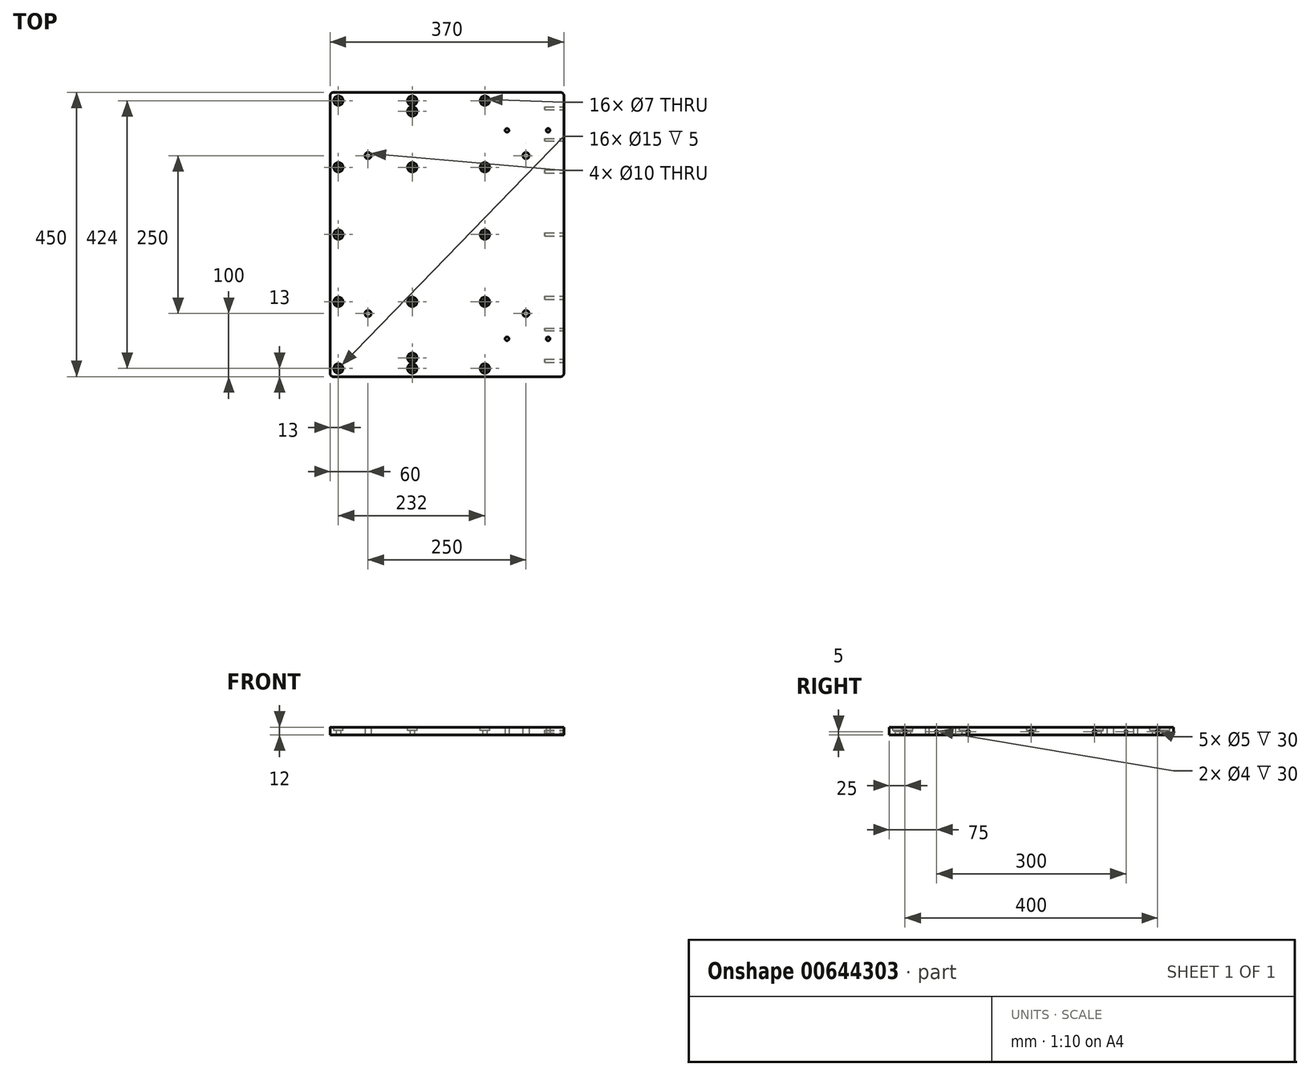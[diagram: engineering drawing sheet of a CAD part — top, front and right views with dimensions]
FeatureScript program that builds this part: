
annotation { "Feature Type Name" : "Feature", "Feature Type Description" : "" }
export const myFeature = defineFeature(function(context is Context, id is Id, definition is map)
    precondition{}
    {
        {
            var Q0;
            Q0=qCreatedBy(makeId("Top.planeOp"),FACE);
            var sketch = newSketch(context, id + "F0", { "sketchPlane" : qUnion([Q0])});
            skLineSegment(sketch, "E0.bottom", {"start": v(185, 225) * mm, "end": v(-185, 225) * mm});
            skLineSegment(sketch, "E0.top", {"start": v(185, -225) * mm, "end": v(-185, -225) * mm});
            skLineSegment(sketch, "E0.left", {"start": v(185, 225) * mm, "end": v(185, -225) * mm});
            skLineSegment(sketch, "E0.right", {"start": v(-185, 225) * mm, "end": v(-185, -225) * mm});
            skPoint(sketch, "E0.middle", {"position": v(0, 0) * mm});
            skLineSegment(sketch, "E1", {"start": v(0, 194.9) * mm, "end": v(0, -168.69) * mm, "construction": true});
            skSolve(sketch);
        }
        {
            var Q0;
            Q0 = qSketchRegion(id + "F0", true);
            extrude(context, id + "F1", {"entities" : qUnion([Q0]), "depth" : 12 * mm, "offsetDistance" : 25 * mm});
        }
        {
            var Q0;
            Q0=qCreatedBy(makeId("Top.planeOp"),FACE);
            var sketch = newSketch(context, id + "F2", { "sketchPlane" : qUnion([Q0])});
            skCircle(sketch, "E2", {"center": v(-172, 106.5) * mm, "radius": 3.5 * mm});
            skCircle(sketch, "E3", {"center": v(-172, 0) * mm, "radius": 3.5 * mm});
            skCircle(sketch, "E4", {"center": v(-172, -332.14) * mm, "radius": 2.87 * mm});
            skLineSegment(sketch, "E5", {"start": v(-172, 212) * mm, "end": v(-172, -289.23) * mm, "construction": true});
            skCircle(sketch, "E6", {"center": v(60, 106.5) * mm, "radius": 3.5 * mm});
            skCircle(sketch, "E7", {"center": v(60, 0) * mm, "radius": 3.5 * mm});
            skCircle(sketch, "E8", {"center": v(60, -212) * mm, "radius": 3.5 * mm});
            skLineSegment(sketch, "E9", {"start": v(60, 212) * mm, "end": v(60, -297.69) * mm, "construction": true});
            skLineSegment(sketch, "E10", {"start": v(213.74, 212) * mm, "end": v(-227.82, 212) * mm, "construction": true});
            skLineSegment(sketch, "E11", {"start": v(213.74, 106.5) * mm, "end": v(-243.05, 106.5) * mm, "construction": true});
            skCircle(sketch, "E12", {"center": v(60, 212) * mm, "radius": 3.5 * mm});
            skCircle(sketch, "E13", {"center": v(-172, 212) * mm, "radius": 3.5 * mm});
            skCircle(sketch, "E14", {"center": v(-172, -106.5) * mm, "radius": 3.5 * mm});
            skCircle(sketch, "E15", {"center": v(-172, -212) * mm, "radius": 3.5 * mm});
            skCircle(sketch, "E16", {"center": v(60, -106.5) * mm, "radius": 3.5 * mm});
            skLineSegment(sketch, "E17", {"start": v(-279.8, -212) * mm, "end": v(194.38, -212) * mm, "construction": true});
            skLineSegment(sketch, "E18", {"start": v(-279.8, -106.5) * mm, "end": v(196.56, -106.5) * mm, "construction": true});
            skCircle(sketch, "E19", {"center": v(-55, 212) * mm, "radius": 3.5 * mm});
            skCircle(sketch, "E20", {"center": v(-55, -212) * mm, "radius": 3.5 * mm});
            skCircle(sketch, "E21", {"center": v(-55, -106.5) * mm, "radius": 3.5 * mm});
            skCircle(sketch, "E22", {"center": v(-55, 106.5) * mm, "radius": 3.5 * mm});
            skLineSegment(sketch, "E23", {"start": v(-55, 255.47) * mm, "end": v(-55, -293.36) * mm, "construction": true});
            skLineSegment(sketch, "E24", {"start": v(-233.42, 165) * mm, "end": v(273.44, 165) * mm, "construction": true});
            skLineSegment(sketch, "E25", {"start": v(-281.7, -165) * mm, "end": v(222.11, -165) * mm, "construction": true});
            skCircle(sketch, "E26", {"center": v(160, -165) * mm, "radius": 3 * mm});
            skCircle(sketch, "E27", {"center": v(160, 165) * mm, "radius": 3 * mm});
            skCircle(sketch, "E28", {"center": v(95, -165) * mm, "radius": 3 * mm});
            skCircle(sketch, "E29", {"center": v(95, 165) * mm, "radius": 3 * mm});
            skLineSegment(sketch, "E30", {"start": v(211.65, 0) * mm, "end": v(-280.45, 0) * mm, "construction": true});
            skCircle(sketch, "E31", {"center": v(-55, 195) * mm, "radius": 3.5 * mm});
            skCircle(sketch, "E32", {"center": v(-55, -195) * mm, "radius": 3.5 * mm});
            skSolve(sketch);
        }
        {
            var Q0;
            Q0 = qSketchRegion(id + "F2", true);
            extrude(context, id + "F3", {"entities" : qUnion([Q0]), "operationType" : NewBodyOperationType.REMOVE, "endBound" : BoundingType.THROUGH_ALL, "depth" : 25 * mm, "offsetDistance" : 25 * mm});
        }
        {
            var Q0;
            Q0=makeQuery(id+"F1.opExtrude","SWEPT_EDGE",EDGE,{"disambiguationData":[OSD([sQuery(id+"F0.wireOp",EDGE,"E0.top"),sQuery(id+"F0.wireOp",EDGE,"E0.right")])]});
            var Q1;
            Q1=makeQuery(id+"F1.opExtrude","SWEPT_EDGE",EDGE,{"disambiguationData":[OSD([sQuery(id+"F0.wireOp",EDGE,"E0.top"),sQuery(id+"F0.wireOp",EDGE,"E0.left")])]});
            var Q2;
            Q2=makeQuery(id+"F1.opExtrude","SWEPT_EDGE",EDGE,{"disambiguationData":[OSD([sQuery(id+"F0.wireOp",EDGE,"E0.bottom"),sQuery(id+"F0.wireOp",EDGE,"E0.left")])]});
            var Q3;
            Q3=makeQuery(id+"F1.opExtrude","SWEPT_EDGE",EDGE,{"disambiguationData":[OSD([sQuery(id+"F0.wireOp",EDGE,"E0.bottom"),sQuery(id+"F0.wireOp",EDGE,"E0.right")])]});
            fillet(context, id + "F4", {"entities" : qUnion([Q0, Q1, Q2, Q3]), "radius" : 5 * mm, "tangentPropagation" : true, "allowEdgeOverflow" : false});
        }
        {
            var Q0;
            Q0=makeQuery(id+"F1.opExtrude","CAP_FACE",FACE,{"disambiguationData":[OSD([sQuery(id+"F0.wireOp",EDGE,"E0.bottom"),sQuery(id+"F0.wireOp",EDGE,"E0.top"),sQuery(id+"F0.wireOp",EDGE,"E0.left"),sQuery(id+"F0.wireOp",EDGE,"E0.right")])],"isStart":false});
            var sketch = newSketch(context, id + "F5", { "sketchPlane" : qUnion([Q0])});
            skCircle(sketch, "E33.0", {"center": v(-172, 212) * mm, "radius": 7.5 * mm});
            skCircle(sketch, "E34.0", {"center": v(-55, 212) * mm, "radius": 7.5 * mm});
            skCircle(sketch, "E35.0", {"center": v(60, 212) * mm, "radius": 7.5 * mm});
            skCircle(sketch, "E36.0", {"center": v(60, 106.5) * mm, "radius": 7.5 * mm});
            skCircle(sketch, "E37.0", {"center": v(-55, 106.5) * mm, "radius": 7.5 * mm});
            skCircle(sketch, "E38.0", {"center": v(-172, 106.5) * mm, "radius": 7.5 * mm});
            skCircle(sketch, "E39.0", {"center": v(-172, 0) * mm, "radius": 7.5 * mm});
            skCircle(sketch, "E40.0", {"center": v(60, 0) * mm, "radius": 7.5 * mm});
            skCircle(sketch, "E41.0", {"center": v(-172, -106.5) * mm, "radius": 7.5 * mm});
            skCircle(sketch, "E42.0", {"center": v(-55, -106.5) * mm, "radius": 7.5 * mm});
            skCircle(sketch, "E43.0", {"center": v(60, -106.5) * mm, "radius": 7.5 * mm});
            skCircle(sketch, "E44.0", {"center": v(60, -212) * mm, "radius": 7.5 * mm});
            skCircle(sketch, "E45.0", {"center": v(-55, -212) * mm, "radius": 7.5 * mm});
            skCircle(sketch, "E46.0", {"center": v(-172, -212) * mm, "radius": 7.5 * mm});
            skCircle(sketch, "E47.0", {"center": v(-55, 195) * mm, "radius": 7.5 * mm});
            skCircle(sketch, "E48.0", {"center": v(-55, -195) * mm, "radius": 7.5 * mm});
            skSolve(sketch);
        }
        {
            var Q0;
            Q0 = qSketchRegion(id + "F5", true);
            extrude(context, id + "F6", {"entities" : qUnion([Q0]), "operationType" : NewBodyOperationType.REMOVE, "oppositeDirection" : true, "depth" : 5 * mm, "offsetDistance" : 25 * mm});
        }
        {
            var Q0;
            Q0=makeQuery(id+"F1.opExtrude","SWEPT_FACE",FACE,{"disambiguationData":[OSD([sQuery(id+"F0.wireOp",EDGE,"E0.left")])]});
            var sketch = newSketch(context, id + "F7", { "sketchPlane" : qUnion([Q0])});
            skCircle(sketch, "E49", {"center": v(100, 5) * mm, "radius": 2.5 * mm});
            skCircle(sketch, "E50", {"center": v(200, 5) * mm, "radius": 2.5 * mm});
            skLineSegment(sketch, "E51", {"start": v(0, 16.7) * mm, "end": v(0, -33.23) * mm, "construction": true});
            skLineSegment(sketch, "E52", {"start": v(-255.46, 5) * mm, "end": v(271.48, 5) * mm, "construction": true});
            skCircle(sketch, "E53.MirrorC", {"center": v(-200, 5) * mm, "radius": 2.5 * mm});
            skCircle(sketch, "E54.MirrorC", {"center": v(-100, 5) * mm, "radius": 2.5 * mm});
            skCircle(sketch, "E55", {"center": v(0, 5) * mm, "radius": 2.5 * mm});
            skPoint(sketch, "E56", {"position": v(-220, 5) * mm});
            skCircle(sketch, "E57", {"center": v(150, 5) * mm, "radius": 2 * mm});
            skCircle(sketch, "E58", {"center": v(-150, 5) * mm, "radius": 2 * mm});
            skSolve(sketch);
        }
        {
            var Q0;
            Q0 = qSketchRegion(id + "F7", true);
            extrude(context, id + "F8", {"entities" : qUnion([Q0]), "operationType" : NewBodyOperationType.REMOVE, "oppositeDirection" : true, "depth" : 30 * mm, "offsetDistance" : 25 * mm});
        }
        {
            var Q0;
            Q0=qCreatedBy(makeId("Top.planeOp"),FACE);
            var sketch = newSketch(context, id + "F9", { "sketchPlane" : qUnion([Q0])});
            skCircle(sketch, "E59", {"center": v(-125, 125) * mm, "radius": 5 * mm});
            skCircle(sketch, "E60", {"center": v(125, 125) * mm, "radius": 5 * mm});
            skCircle(sketch, "E61", {"center": v(-125, -125) * mm, "radius": 5 * mm});
            skCircle(sketch, "E62", {"center": v(125, -125) * mm, "radius": 5 * mm});
            skSolve(sketch);
        }
        {
            var Q0;
            Q0 = qSketchRegion(id + "F9", true);
            extrude(context, id + "F10", {"entities" : qUnion([Q0]), "operationType" : NewBodyOperationType.REMOVE, "endBound" : BoundingType.THROUGH_ALL, "depth" : 25 * mm, "offsetDistance" : 25 * mm});
        }
    });
